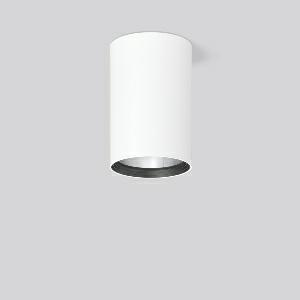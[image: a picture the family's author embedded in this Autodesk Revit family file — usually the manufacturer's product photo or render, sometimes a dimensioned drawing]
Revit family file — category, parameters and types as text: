
# Revit family: heledon_maxi_a_931218_002_1_1b7c
name_source: partatom
category: Lighting Fixtures
units: mm (PartAtom-declared; Revit-internal decimal feet)

## family parameters
Cut with Voids When Loaded = No
Host = Face
Light Source = No
Part Type = Normal
Room Calculation Point = No
Round Connector Dimension = Use Diameter
Shared = No

## types (1)
- HELEDON maxi A (1 x LED Modul 940, 3500 lm, 4000)
    Apparent Load = 25 VA
    Approval mark = CE
    CIE Flux Codes = 100 100 100 100 100
    Color Rendering = 92
    Color Temperature = 4000
    Default Elevation = 1800 mm
    Description = Series: HELEDON maxi
Cylindrical surface-mounted downlight. Housing: die-cast aluminium, powder-coated. Internal ceiling frame polycarbonate with bayonet mounting. Black plastic ring and recessed LED to prevent glare from the side. Optical assembly with reflector made of MIRO-Silver with 98% total light reflection for outstanding efficiency - can be changed without tools. Best colour rendering index Ra>90. Suitable for Ceiling mounting. Easy installation with a separate ceiling frame with bayonet mounting and plug connection. Driver integrated. Connected via plug-in connector. High quality converter without flickering and stroboscopic effect. The following accessories can be mounted without use of tools: interchangeable lenses, decorative glasses, honeycomb louvre, clear and frosted diffusers, white interchangeable plastic ring. 
Colour: traffic white, matt (RAL 9016)
Diameter: 123 mm
Height: 183 mm
Lamp: LED
Socket: without socket
Colour temperature: 4000K
Colour rendering index (CRI): 92
System power: 25 W
Rated luminous flux: 3500 lm
Luminous efficiency: 140 lm/W
Control gear: Regulated power supply
Protection class: I
Type of protection: IP 20
    Height = 183 mm
    Lamp = 1 x LED Modul 940
    Lamp Light Flux = 3500 lm
    Lamp count = 1
    Length = 123 mm
    Lifetime = 50000 h
    Luminous efficacy = 140 lm/W
    Manufacturer = RZB
    ModVariant = No
    Model = 931218.002.1
    Mounting Place = Ceiling
    Mounting Type = Surface mounted
    Number of Poles = 1
    OnlyDefault = Yes
    Power Factor = 1
    Product Name = HELEDON maxi A
    Product group = Surface mounted downlights
    ProductGroupID = 302
    Protection Class = Protection class I
    Protection Degree = IP 20
    RLX_Detail_Level = 1
    RLX_Emergency_Light_Flux = 0 lm
    RLX_Emergency_Type = 0
    RLX_Emergency_Type_DB = No
    RlxData = <blob elided: 97289 chars, md5=b98a20e1>
    Socket = socket
    Standby Power = 0 W
    System Light Flux = 3500 lm
    System Power = 25 W
    Type Comments = Product without accessories
    Type Image = 931192.002.jpg
    URL = http://relux.com
    VarID = ---
    Voltage = 230 V
    Voltage Range = 220-240 V
    Weight = 0.00 kg
    Width = 0 mm  [stored 0 ft]

note: [stored X ft] marks values corroborated as IEEE doubles in the binary element streams (Revit-internal decimal feet)

## geometry (parser evidence)
native form markers: Blend x4, Sweep x11
no freeform markers — native parametric forms only
